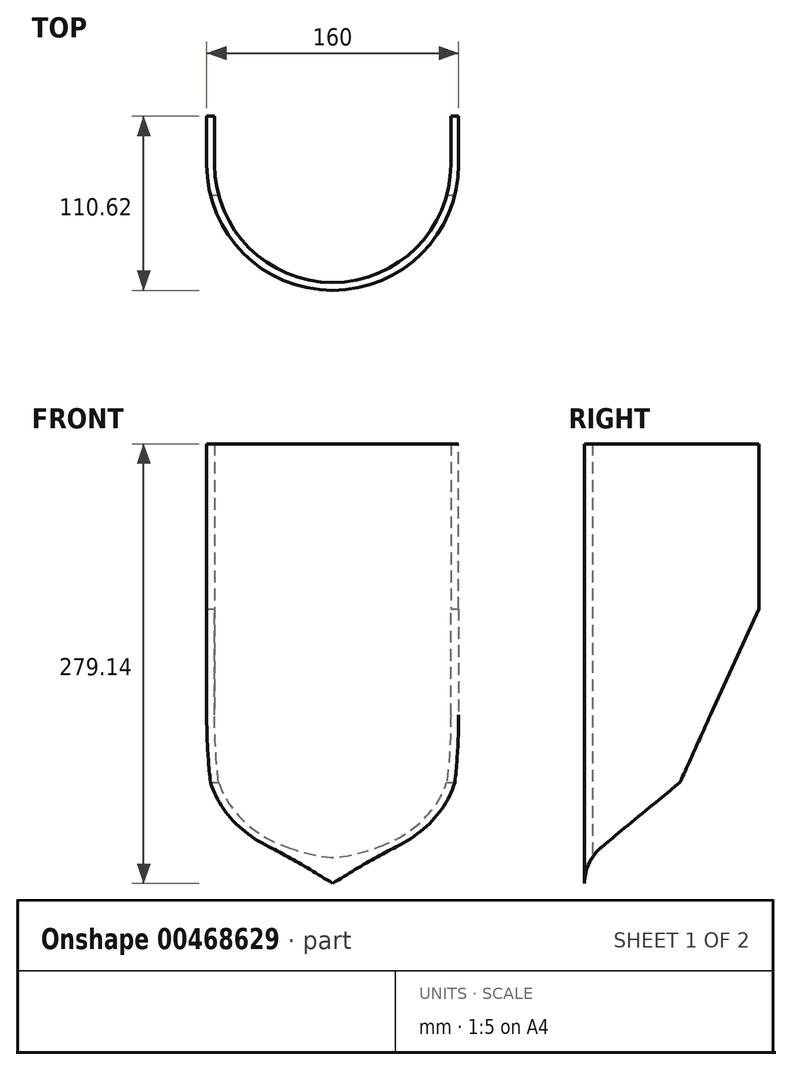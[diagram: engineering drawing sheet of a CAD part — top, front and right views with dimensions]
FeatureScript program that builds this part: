
annotation { "Feature Type Name" : "Feature", "Feature Type Description" : "" }
export const myFeature = defineFeature(function(context is Context, id is Id, definition is map)
    precondition{}
    {
        {
            var Q0;
            Q0=qCreatedBy(makeId("Top.planeOp"),FACE);
            var sketch = newSketch(context, id + "F0", { "sketchPlane" : qUnion([Q0]) });
            skLineSegment(sketch, "E0.top", {"start": v(80, 140.61) * mm, "end": v(75, 140.61) * mm});
            skLineSegment(sketch, "E0.left", {"start": v(80, 80) * mm, "end": v(80, 140.61) * mm});
            skLineSegment(sketch, "E0.right", {"start": v(-80, 80) * mm, "end": v(-80, 140.62) * mm});
            skLineSegment(sketch, "E1", {"start": v(-75, 140.62) * mm, "end": v(-75, 80) * mm});
            skLineSegment(sketch, "E2", {"start": v(75, 140.61) * mm, "end": v(75, 80) * mm});
            skLineSegment(sketch, "E3.trimOffspring", {"start": v(-75, 140.62) * mm, "end": v(-80, 140.62) * mm});
            skPoint(sketch, "E4.orphan", {"position": v(-75, 0.62) * mm});
            skPoint(sketch, "E5.orphan", {"position": v(75, 0.62) * mm});
            skPoint(sketch, "E6.visualSharp", {"position": v(-75, 5.62) * mm});
            skPoint(sketch, "E7.visualSharp", {"position": v(75, 5.62) * mm});
            skPoint(sketch, "E8.visualSharp", {"position": v(-80, 0.62) * mm});
            skPoint(sketch, "E9.visualSharp", {"position": v(80, 0.62) * mm});
            skArc(sketch, "E10", {"start": v(-80, 80) * mm, "mid": v(0, 0) * mm, "end": v(80, 80) * mm});
            skPoint(sketch, "E10.first.point", {"position": v(0, 0) * mm});
            skPoint(sketch, "E10.second.point", {"position": v(80, 80) * mm});
            skPoint(sketch, "E10.third.point", {"position": v(-80, 80) * mm});
            skArc(sketch, "E11", {"start": v(-75, 80) * mm, "mid": v(0, 5) * mm, "end": v(75, 80) * mm});
            skPoint(sketch, "E11.first.point", {"position": v(0.06, 5) * mm});
            skPoint(sketch, "E11.second.point", {"position": v(75, 80) * mm});
            skPoint(sketch, "E11.third.point", {"position": v(-75, 80) * mm});
            skSolve(sketch);
        }
        {
            var Q0;
            Q0=qSketchRegion(id+"F0",true);
            extrude(context, id + "F1", {"entities" : qUnion([Q0]), "endBound" : BoundingType.SYMMETRIC, "depth" : 540 * mm, "offsetDistance" : 25 * mm});
        }
        {
            var Q0;
            Q0=qCreatedBy(makeId("Right.planeOp"),FACE);
            var sketch = newSketch(context, id + "F2", { "sketchPlane" : qUnion([Q0]) });
            skPoint(sketch, "E12.visualSharp", {"position": v(140.62, 270) * mm});
            skLineSegment(sketch, "E13.bottom", {"start": v(140.62, 270) * mm, "end": v(0, 270) * mm});
            skLineSegment(sketch, "E13.top", {"start": v(140.62, 270) * mm, "end": v(0, 270) * mm});
            skLineSegment(sketch, "E13.left", {"start": v(140.62, 270) * mm, "end": v(140.62, 270) * mm});
            skLineSegment(sketch, "E13.right", {"start": v(0, 270) * mm, "end": v(0, 270) * mm});
            skLineSegment(sketch, "E14", {"start": v(60.62, 5) * mm, "end": v(110.62, 115.19) * mm});
            skLineSegment(sketch, "E15", {"start": v(60.62, 5) * mm, "end": v(10.91, -36) * mm});
            skLineSegment(sketch, "E16", {"start": v(140.62, -270) * mm, "end": v(0, -270) * mm});
            skLineSegment(sketch, "E17", {"start": v(0, -270) * mm, "end": v(0, -59.14) * mm});
            skLineSegment(sketch, "E18", {"start": v(0, 270) * mm, "end": v(0, 220) * mm});
            skLineSegment(sketch, "E19", {"start": v(110.62, 220) * mm, "end": v(110.62, 115.19) * mm});
            skLineSegment(sketch, "E20.trimOffspring", {"start": v(110.62, 220) * mm, "end": v(0, 220) * mm});
            skLineSegment(sketch, "E21", {"start": v(140.62, 270) * mm, "end": v(140.62, -270) * mm});
            skPoint(sketch, "E22.visualSharp", {"position": v(0, -45) * mm});
            skArc(sketch, "E22.filletArc", {"start": v(10.91, -36) * mm, "mid": v(2.86, -46.35) * mm, "end": v(0, -59.14) * mm});
            skSolve(sketch);
        }
        {
            var Q0;
            Q0=qSketchRegion(id+"F2",true);
            extrude(context, id + "F3", {"entities" : qUnion([Q0]), "operationType" : NewBodyOperationType.REMOVE, "endBound" : BoundingType.SYMMETRIC, "oppositeDirection" : true, "depth" : 500 * mm});
        }
    });
